# Revit family: STH9910BRPTO_STH9910PTO
name_source: partatom
category: Luminárias
units: mm (PartAtom-declared; Revit-internal decimal feet)

## family parameters
Compartilhado = Não
Corte com vazios quando carregada = Não
Cota do conector redondo = Utilizar diâmetro
Fonte luminosa = Não
Hospedeiro = Forro
Manter orientação da anotação = Não
Número OmniClass = 23.80.70.11
Ponto de cálculo do ambiente = Não
Sempre na vertical = Sim
Tipo de parte = Normal
Título OmniClass = Luminaries for Internal Lighting

## types (2) — shared parameters
Altura = 0.06 m
Comentários de tipos = Lâmpada indicada: 1x MR16 GU10 Stella
Comprimento = 0.05 m
Fabricante = Stella
Largura = 0.05 m
Modelo = Narrow MR11
Potência máxima = 15 W
Tensão Elétrica = 127V-220V
URL = https://stella.com.br
Ângulo de Abertura = 20°
zero-valued in all types: Elevação padrão

## per-type parameters (varying)
| type | Base | Referência |
| STH9910BR/PTO - BIVOLT - 20° | Al - Branco | STH9910BR/PTO |
| STH9910/PTO - BIVOLT - 20° | Al - Preto | STH9910/PTO |
